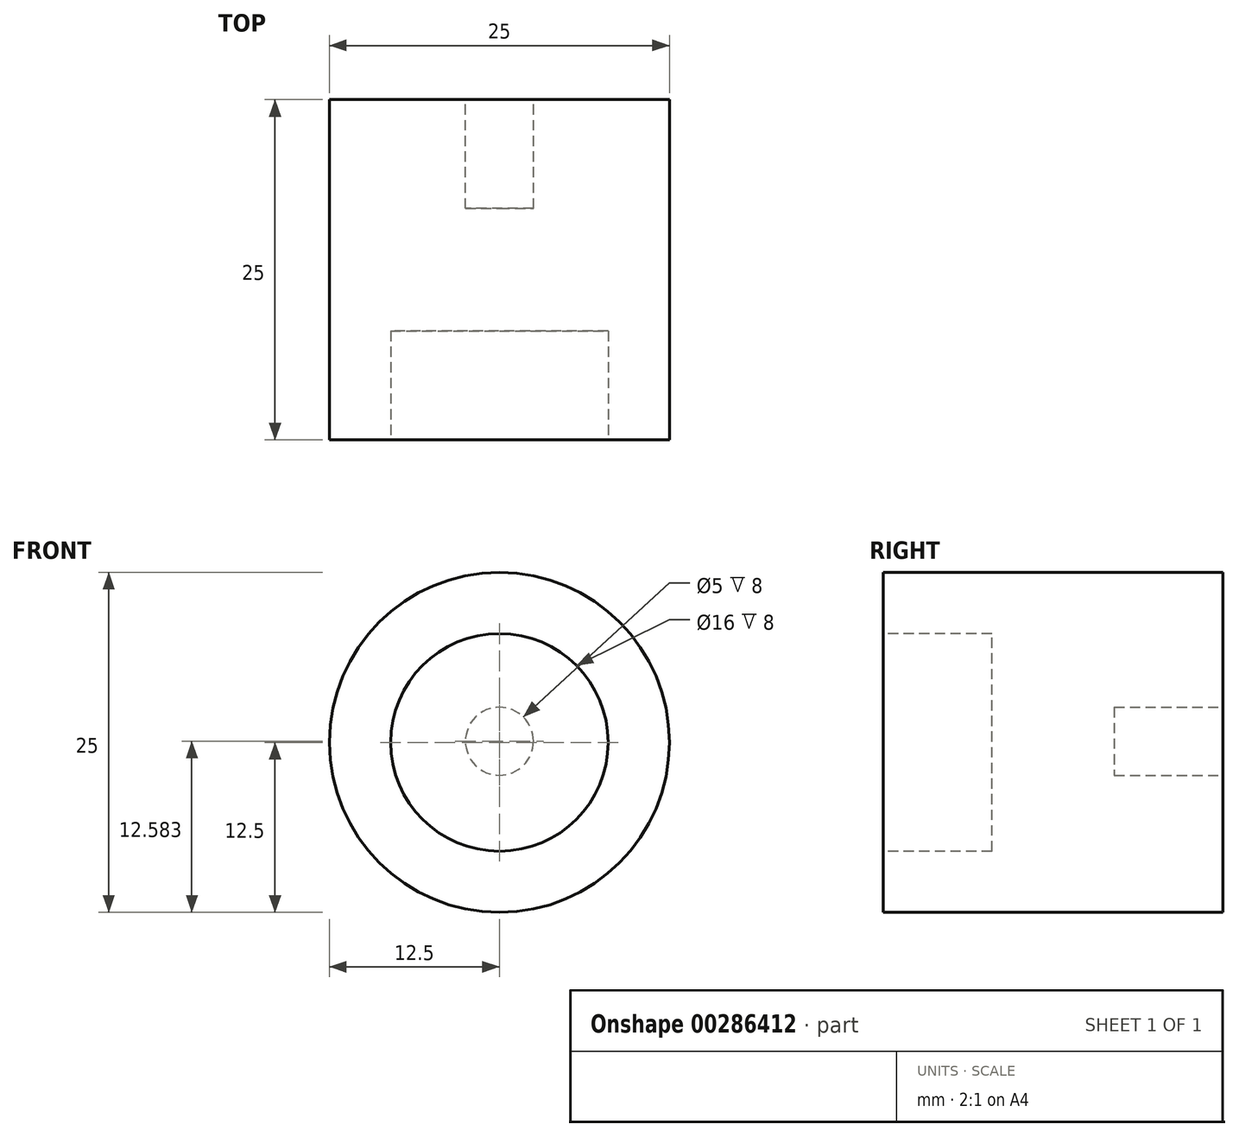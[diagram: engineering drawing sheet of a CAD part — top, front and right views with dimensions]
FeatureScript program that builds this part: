
annotation { "Feature Type Name" : "Feature", "Feature Type Description" : "" }
export const myFeature = defineFeature(function(context is Context, id is Id, definition is map)
    precondition{}
    {
        {
            var Q0;
            Q0=qCreatedBy(makeId("Front.planeOp"),FACE);
            var sketch = newSketch(context, id + "F0", { "sketchPlane" : qUnion([Q0])});
            skCircle(sketch, "E0", {"center": v(0, 0) * mm, "radius": 12.5 * mm});
            skSolve(sketch);
        }
        {
            var Q0;
            Q0 = qSketchRegion(id + "F0", true);
            var Q1;
            Q1=sQuery(id+"F0.wireOp",EDGE,"E0");
            extrude(context, id + "F1", {"entities" : qUnion([Q0]), "surfaceEntities" : qUnion([Q1]), "depth" : 25 * mm});
        }
        {
            var Q0;
            Q0=makeQuery(id+"F1.opExtrude","CAP_FACE",FACE,{"disambiguationData":[OSD([sQuery(id+"F0.wireOp",EDGE,"E0")])],"isStart":true});
            var sketch = newSketch(context, id + "F2", { "sketchPlane" : qUnion([Q0])});
            skCircle(sketch, "E1", {"center": v(0, 0.08) * mm, "radius": 2.5 * mm});
            skSolve(sketch);
        }
        {
            var Q0;
            Q0=makeQuery(id+"F2.imprint","IMPRINT",FACE,{"disambiguationData":[TD([[makeQuery(id+"F2.imprint","IMPRINT",EDGE,{"derivedFrom":sQuery(id+"F2.wireOp",EDGE,"E1")}),1.0]])]});
            var Q1;
            Q1=sQuery(id+"F2.wireOp",EDGE,"E1");
            extrude(context, id + "F3", {"entities" : qUnion([Q0]), "operationType" : NewBodyOperationType.REMOVE, "surfaceEntities" : qUnion([Q1]), "oppositeDirection" : true, "depth" : 8 * mm});
        }
        {
            var Q0;
            Q0=makeQuery(id+"F1.opExtrude","CAP_FACE",FACE,{"disambiguationData":[OSD([sQuery(id+"F0.wireOp",EDGE,"E0")])],"isStart":false});
            var sketch = newSketch(context, id + "F4", { "sketchPlane" : qUnion([Q0])});
            skCircle(sketch, "E2", {"center": v(0, 0) * mm, "radius": 8 * mm});
            skSolve(sketch);
        }
        {
            var Q0;
            Q0 = qSketchRegion(id + "F4", true);
            extrude(context, id + "F5", {"entities" : qUnion([Q0]), "operationType" : NewBodyOperationType.REMOVE, "oppositeDirection" : true, "depth" : 8 * mm});
        }
    });
